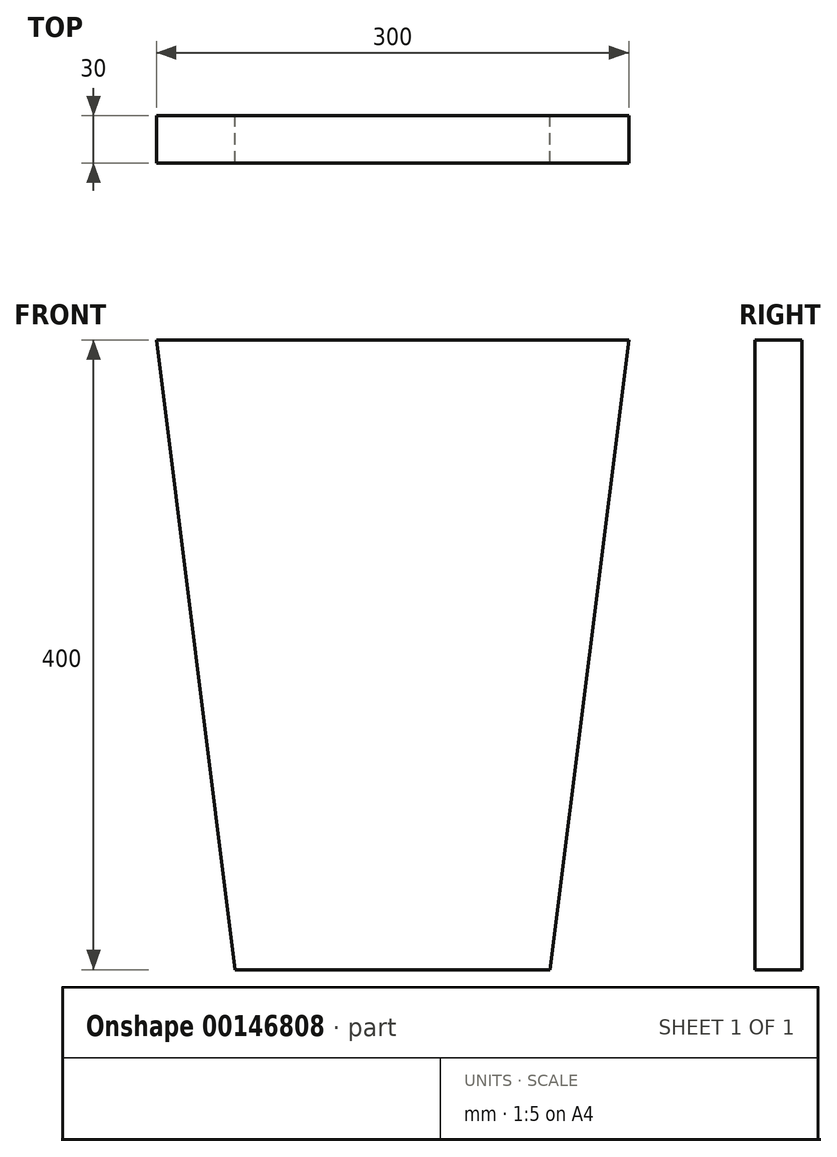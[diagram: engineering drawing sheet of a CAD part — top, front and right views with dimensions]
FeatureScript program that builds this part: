
annotation { "Feature Type Name" : "Feature", "Feature Type Description" : "" }
export const myFeature = defineFeature(function(context is Context, id is Id, definition is map)
    precondition{}
    {
        {
            var Q0;
            Q0=qCreatedBy(makeId("Front.planeOp"),FACE);
            var sketch = newSketch(context, id + "F0", { "sketchPlane" : qUnion([Q0])});
            skLineSegment(sketch, "E0", {"start": v(-150, 36.3) * mm, "end": v(150, 36.3) * mm});
            skLineSegment(sketch, "E1", {"start": v(-100, -363.7) * mm, "end": v(100, -363.7) * mm});
            skPoint(sketch, "E2", {"position": v(0, 36.3) * mm});
            skPoint(sketch, "E3", {"position": v(0, -363.7) * mm});
            skLineSegment(sketch, "E4", {"start": v(-150, 36.3) * mm, "end": v(-100, -363.7) * mm});
            skLineSegment(sketch, "E5", {"start": v(150, 36.3) * mm, "end": v(100, -363.7) * mm});
            skSolve(sketch);
        }
        {
            var Q0;
            Q0=makeQuery(id+"F0.imprint","IMPRINT",FACE,{"disambiguationData":[TD([[makeQuery(id+"F0.imprint","IMPRINT",EDGE,{"derivedFrom":sQuery(id+"F0.wireOp",EDGE,"E0")}),-1.0]])]});
            extrude(context, id + "F1", {"entities" : qUnion([Q0]), "depth" : 30 * mm});
        }
    });
